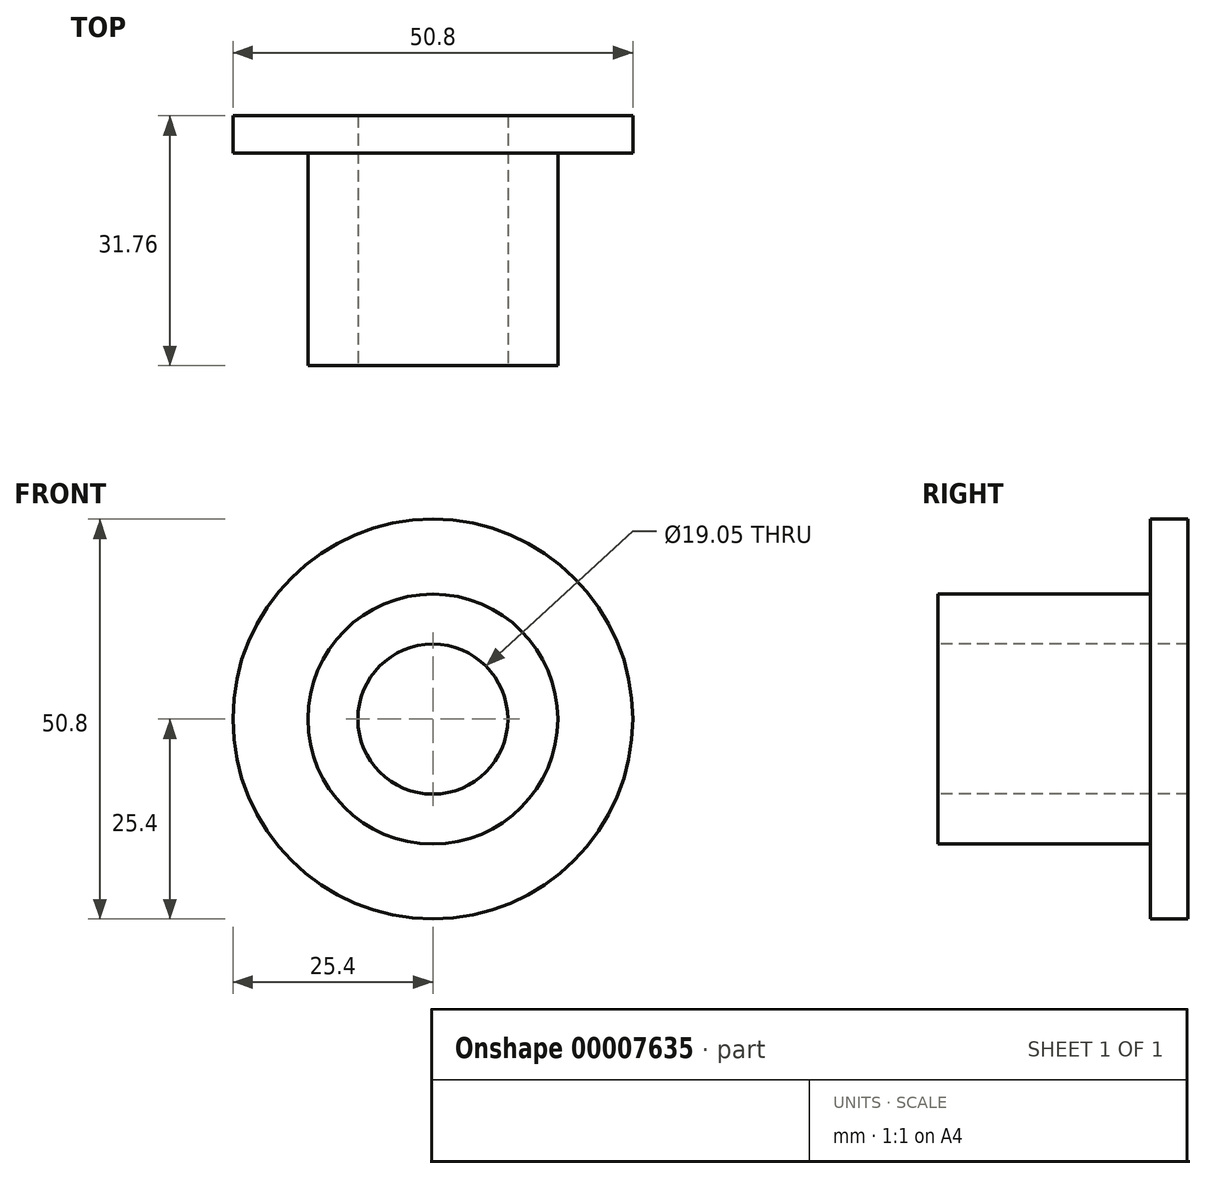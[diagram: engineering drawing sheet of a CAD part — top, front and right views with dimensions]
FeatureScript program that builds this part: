
annotation { "Feature Type Name" : "Feature", "Feature Type Description" : "" }
export const myFeature = defineFeature(function(context is Context, id is Id, definition is map)
    precondition{}
    {
        {
            var Q0;
            Q0=qCreatedBy(makeId("Right.planeOp"),FACE);
            var sketch = newSketch(context, id + "F0", { "sketchPlane" : qUnion([Q0])});
            skLineSegment(sketch, "E0", {"start": v(-15.88, 0) * mm, "end": v(15.88, 0) * mm, "construction": true});
            skLineSegment(sketch, "E1", {"start": v(-15.88, 15.88) * mm, "end": v(-15.88, 9.52) * mm});
            skLineSegment(sketch, "E2", {"start": v(-15.88, 9.52) * mm, "end": v(15.88, 9.53) * mm});
            skLineSegment(sketch, "E3", {"start": v(15.88, 9.52) * mm, "end": v(15.88, 25.4) * mm});
            skLineSegment(sketch, "E4", {"start": v(15.88, 25.4) * mm, "end": v(11.11, 25.4) * mm});
            skLineSegment(sketch, "E5", {"start": v(11.11, 25.4) * mm, "end": v(11.11, 15.88) * mm});
            skLineSegment(sketch, "E6", {"start": v(11.11, 15.88) * mm, "end": v(-15.88, 15.87) * mm});
            skSolve(sketch);
        }
        {
            var Q0;
            Q0 = qSketchRegion(id + "F0", true);
            var Q1;
            Q1=sQuery(id+"F0.wireOp",EDGE,"E0");
            revolve(context, id + "F1", {"entities" : qUnion([Q0]), "axis" : qUnion([Q1]), "revolveType" : RevolveType.FULL});
        }
    });
